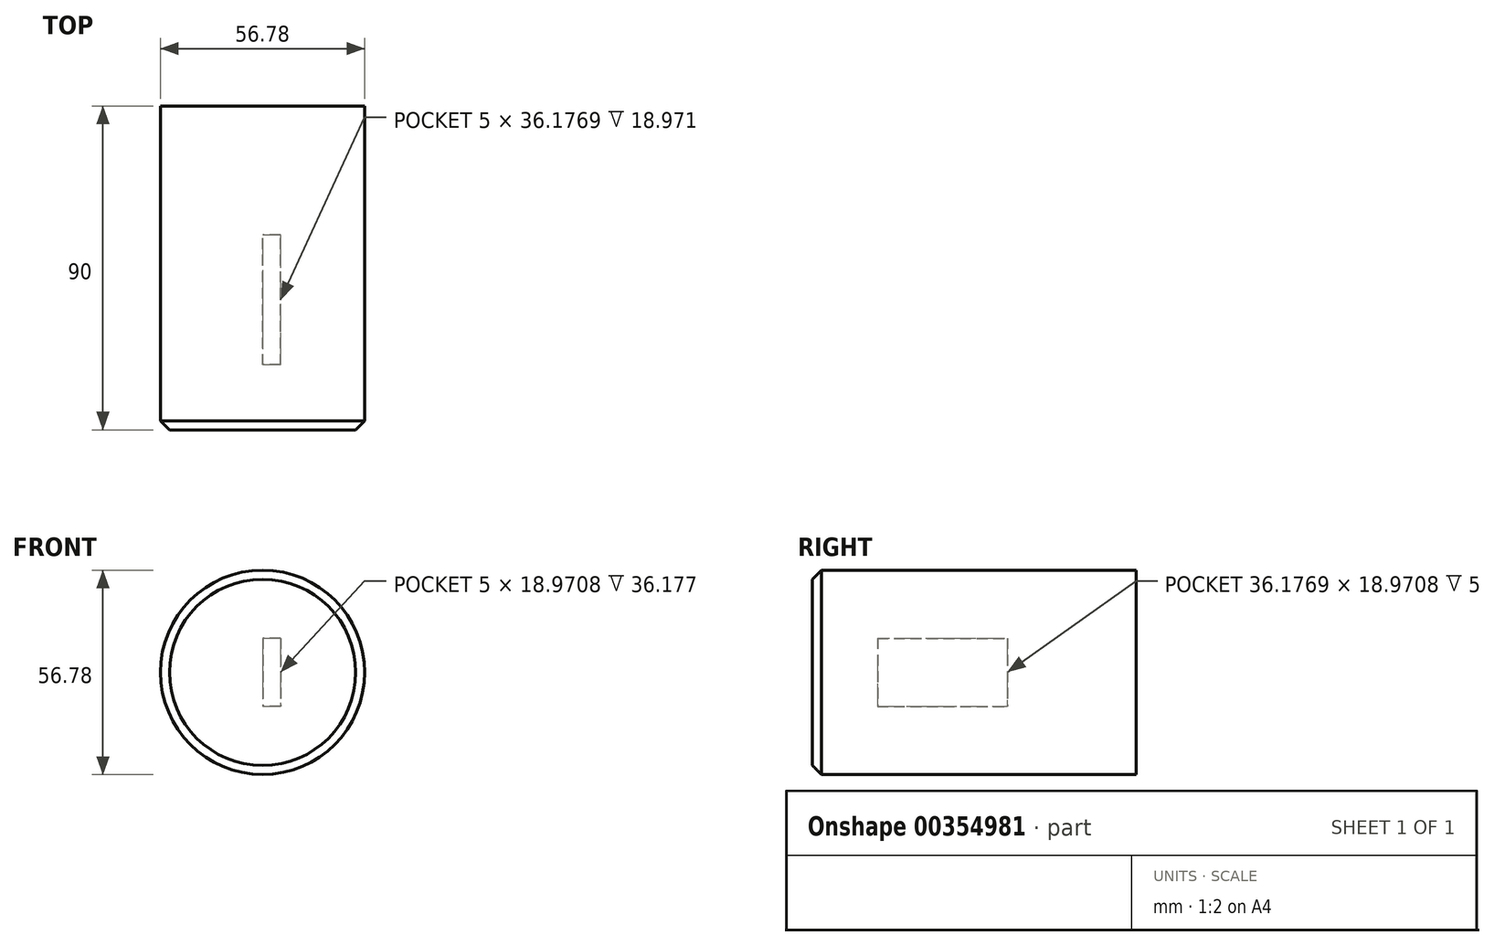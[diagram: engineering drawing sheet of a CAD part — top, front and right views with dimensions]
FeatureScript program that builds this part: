
annotation { "Feature Type Name" : "Feature", "Feature Type Description" : "" }
export const myFeature = defineFeature(function(context is Context, id is Id, definition is map)
    precondition{}
    {
        {
            var Q0;
            Q0=qCreatedBy(makeId("Front.planeOp"),FACE);
            var sketch = newSketch(context, id + "F0", { "sketchPlane" : qUnion([Q0])});
            skCircle(sketch, "E0", {"center": v(0, 0) * mm, "radius": 28.39 * mm});
            skSolve(sketch);
        }
        {
            var Q0;
            Q0 = qSketchRegion(id + "F0", true);
            extrude(context, id + "F1", {"entities" : qUnion([Q0]), "depth" : 90 * mm});
        }
        {
            var Q0;
            Q0=makeQuery(id+"F1.opExtrude","CAP_EDGE",EDGE,{"disambiguationData":[OSD([sQuery(id+"F0.wireOp",EDGE,"E0")])],"isStart":false});
            chamfer(context, id + "F2", {"entities" : qUnion([Q0]), "width" : 2.5 * mm, "tangentPropagation" : true});
        }
        {
            var Q0;
            Q0=qCreatedBy(makeId("Right.planeOp"),FACE);
            var sketch = newSketch(context, id + "F3", { "sketchPlane" : qUnion([Q0])});
            skLineSegment(sketch, "E1.bottom", {"start": v(-71.91, 9.49) * mm, "end": v(-35.74, 9.49) * mm});
            skLineSegment(sketch, "E1.top", {"start": v(-71.91, -9.49) * mm, "end": v(-35.74, -9.49) * mm});
            skLineSegment(sketch, "E1.left", {"start": v(-71.91, 9.49) * mm, "end": v(-71.91, -9.49) * mm});
            skLineSegment(sketch, "E1.right", {"start": v(-35.74, 9.49) * mm, "end": v(-35.74, -9.49) * mm});
            skPoint(sketch, "E1.middle", {"position": v(-53.82, 0) * mm});
            skSolve(sketch);
        }
        {
            var Q0;
            Q0 = qSketchRegion(id + "F3", true);
            extrude(context, id + "F4", {"entities" : qUnion([Q0]), "operationType" : NewBodyOperationType.REMOVE, "depth" : 5 * mm});
        }
    });
